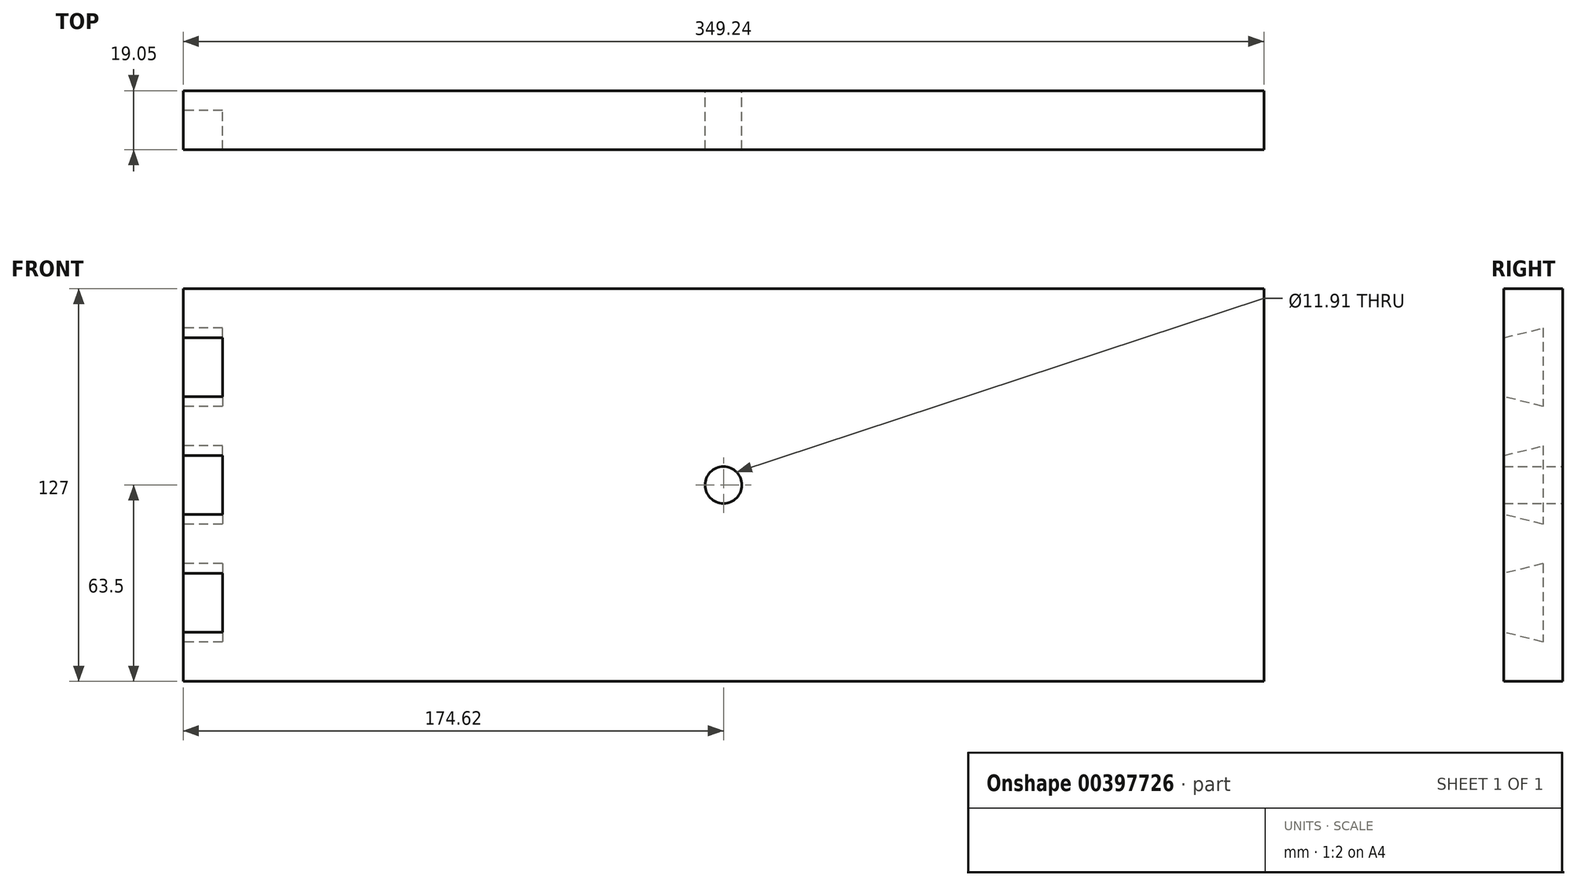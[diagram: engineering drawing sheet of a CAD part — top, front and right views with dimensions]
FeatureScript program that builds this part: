
annotation { "Feature Type Name" : "Feature", "Feature Type Description" : "" }
export const myFeature = defineFeature(function(context is Context, id is Id, definition is map)
    precondition{}
    {
        {
            var Q0;
            Q0=qCreatedBy(makeId("Front.planeOp"),FACE);
            var sketch = newSketch(context, id + "F0", { "sketchPlane" : qUnion([Q0])});
            skLineSegment(sketch, "E0.bottom", {"start": v(-174.62, -63.5) * mm, "end": v(174.62, -63.5) * mm});
            skLineSegment(sketch, "E0.top", {"start": v(-174.62, 63.5) * mm, "end": v(174.62, 63.5) * mm});
            skLineSegment(sketch, "E0.left", {"start": v(-174.63, -63.5) * mm, "end": v(-174.63, 63.5) * mm});
            skLineSegment(sketch, "E0.right", {"start": v(174.63, -63.5) * mm, "end": v(174.63, 63.5) * mm});
            skLineSegment(sketch, "E1", {"start": v(-174.63, 0) * mm, "end": v(0, 0) * mm, "construction": true});
            skPoint(sketch, "E2", {"position": v(0, 0) * mm});
            skLineSegment(sketch, "E3", {"start": v(0, 0) * mm, "end": v(0, 63.5) * mm, "construction": true});
            skSolve(sketch);
        }
        {
            var Q0;
            Q0=makeQuery(id+"F0.imprint","IMPRINT",FACE,{"disambiguationData":[TD([[makeQuery(id+"F0.imprint","IMPRINT",EDGE,{"derivedFrom":sQuery(id+"F0.wireOp",EDGE,"E0.bottom")}),1.0]])]});
            extrude(context, id + "F1", {"entities" : qUnion([Q0]), "depth" : 19.05 * mm});
        }
        {
            var Q0;
            Q0=makeQuery(id+"F1.opExtrude","SWEPT_FACE",FACE,{"disambiguationData":[OSD([sQuery(id+"F0.wireOp",EDGE,"E0.left")])]});
            var sketch = newSketch(context, id + "F2", { "sketchPlane" : qUnion([Q0])});
            skLineSegment(sketch, "E4", {"start": v(19.05, 47.62) * mm, "end": v(6.35, 50.8) * mm});
            skLineSegment(sketch, "E5", {"start": v(6.35, 50.8) * mm, "end": v(6.35, 25.4) * mm});
            skLineSegment(sketch, "E6", {"start": v(6.35, -50.8) * mm, "end": v(19.05, -47.62) * mm});
            skLineSegment(sketch, "E7", {"start": v(19.05, -47.62) * mm, "end": v(19.05, -28.58) * mm});
            skLineSegment(sketch, "E8", {"start": v(6.35, 25.4) * mm, "end": v(19.05, 28.57) * mm});
            skLineSegment(sketch, "E9", {"start": v(19.05, 9.52) * mm, "end": v(6.35, 12.7) * mm});
            skLineSegment(sketch, "E10", {"start": v(6.35, -12.7) * mm, "end": v(19.05, -9.53) * mm});
            skLineSegment(sketch, "E11", {"start": v(6.35, -25.4) * mm, "end": v(19.05, -28.58) * mm});
            skLineSegment(sketch, "E12.trimOffspring", {"start": v(19.05, 28.57) * mm, "end": v(19.05, 47.62) * mm});
            skLineSegment(sketch, "E13.trimOffspring", {"start": v(6.35, 12.7) * mm, "end": v(6.35, -12.7) * mm});
            skLineSegment(sketch, "E14.trimOffspring", {"start": v(6.35, -25.4) * mm, "end": v(6.35, -50.8) * mm});
            skLineSegment(sketch, "E15.trimOffspring", {"start": v(19.05, -9.53) * mm, "end": v(19.05, 9.52) * mm});
            skLineSegment(sketch, "E16", {"start": v(6.35, -25.4) * mm, "end": v(6.35, -12.7) * mm, "construction": true});
            skLineSegment(sketch, "E17.trimOffspring", {"start": v(6.35, 12.7) * mm, "end": v(6.35, 25.4) * mm, "construction": true});
            skPoint(sketch, "E18", {"position": v(6.35, 19.05) * mm});
            skPoint(sketch, "E19", {"position": v(6.35, -19.05) * mm});
            skLineSegment(sketch, "E20", {"start": v(0, 57.15) * mm, "end": v(19.05, 57.15) * mm, "construction": true});
            skLineSegment(sketch, "E21", {"start": v(6.35, -50.8) * mm, "end": v(6.35, -63.5) * mm, "construction": true});
            skLineSegment(sketch, "E22", {"start": v(6.35, -57.15) * mm, "end": v(19.05, -57.15) * mm, "construction": true});
            skSolve(sketch);
        }
        {
            var Q0;
            Q0=makeQuery(id+"F2.imprint","IMPRINT",FACE,{"disambiguationData":[TD([[makeQuery(id+"F2.imprint","IMPRINT",EDGE,{"derivedFrom":sQuery(id+"F2.wireOp",EDGE,"E6")}),1.0]])]});
            var Q1;
            Q1=makeQuery(id+"F2.imprint","IMPRINT",FACE,{"disambiguationData":[TD([[makeQuery(id+"F2.imprint","IMPRINT",EDGE,{"derivedFrom":sQuery(id+"F2.wireOp",EDGE,"E9")}),1.0]])]});
            var Q2;
            Q2=makeQuery(id+"F2.imprint","IMPRINT",FACE,{"disambiguationData":[TD([[makeQuery(id+"F2.imprint","IMPRINT",EDGE,{"derivedFrom":sQuery(id+"F2.wireOp",EDGE,"E4")}),1.0]])]});
            extrude(context, id + "F3", {"entities" : qUnion([Q0, Q1, Q2]), "operationType" : NewBodyOperationType.REMOVE, "oppositeDirection" : true, "depth" : 12.7 * mm});
        }
        {
            var Q0;
            Q0=sQuery(id+"F0.wireOp",VERTEX,"E2");
            var Q1;
            Q1=makeQuery(id+"F1.opExtrude","SWEPT_BODY",BODY,{"disambiguationData":[OSD([sQuery(id+"F0.wireOp",EDGE,"E0.bottom"),sQuery(id+"F0.wireOp",EDGE,"E0.top"),sQuery(id+"F0.wireOp",EDGE,"E0.left"),sQuery(id+"F0.wireOp",EDGE,"E0.right")])]});
            hole(context, id + "F4", {"style" : HoleStyle.SIMPLE, "endStyle" : HoleEndStyle.BLIND, "oppositeDirection" : true, "holeDiameter" : 11.9 * mm, "holeDepth" : 34.92 * mm, "tappedDepth" : 12.7 * mm, "tapClearance" : 3, "locations" : qUnion([Q0]), "scope" : qUnion([Q1])});
        }
    });
